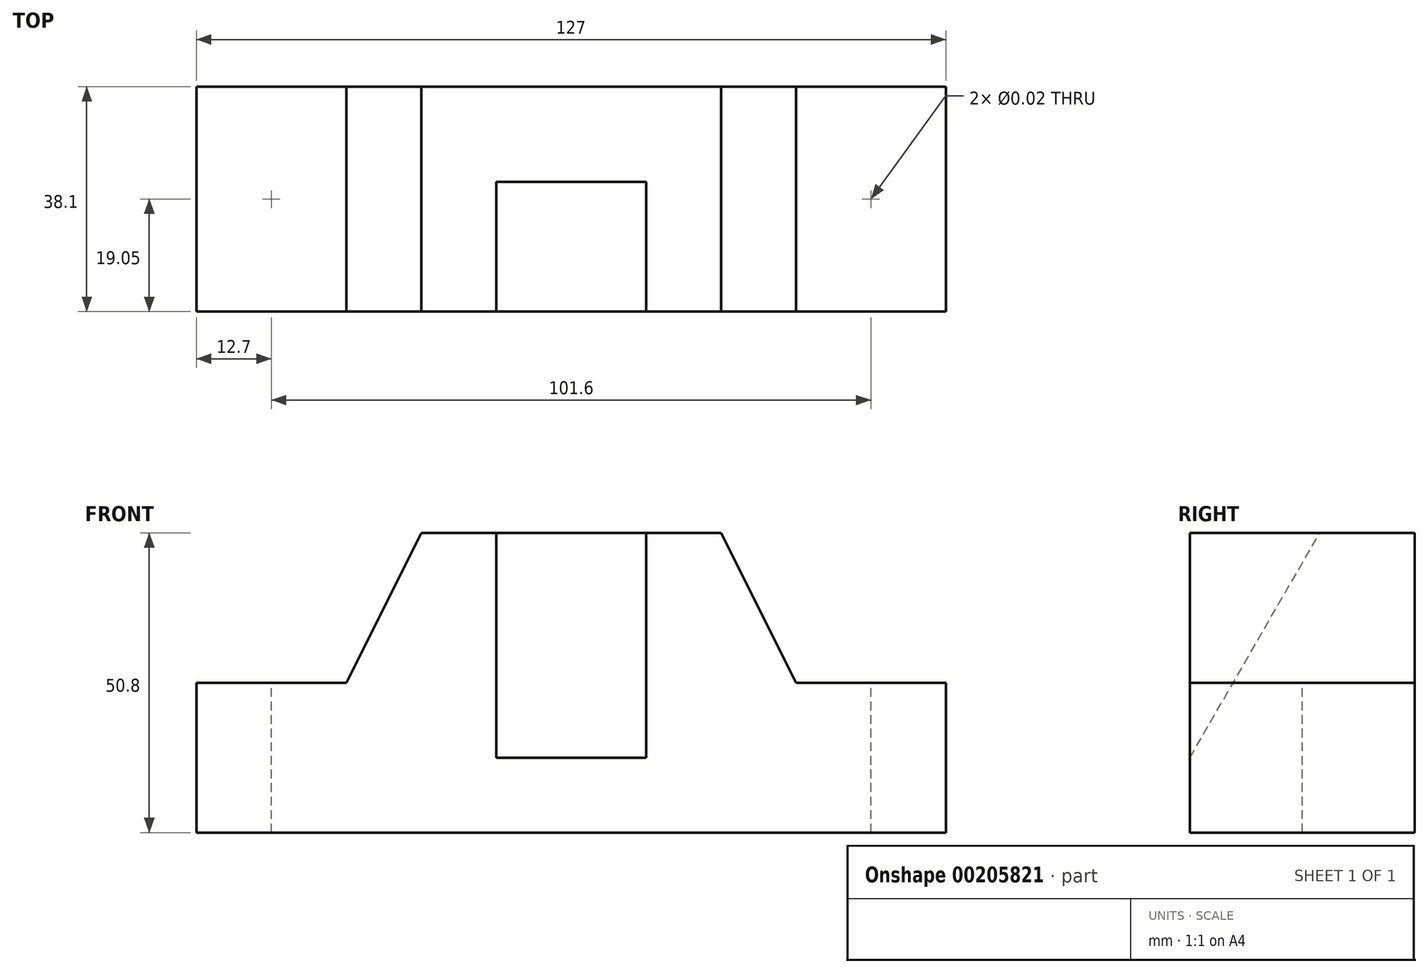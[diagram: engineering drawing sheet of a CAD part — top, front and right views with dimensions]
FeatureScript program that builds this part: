
annotation { "Feature Type Name" : "Feature", "Feature Type Description" : "" }
export const myFeature = defineFeature(function(context is Context, id is Id, definition is map)
    precondition{}
    {
        {
            var Q0;
            Q0=qCreatedBy(makeId("Front.planeOp"),FACE);
            var sketch = newSketch(context, id + "F0", { "sketchPlane" : qUnion([Q0])});
            skLineSegment(sketch, "E0", {"start": v(63.5, 0) * mm, "end": v(-63.5, 0) * mm});
            skLineSegment(sketch, "E1", {"start": v(-63.5, 0) * mm, "end": v(-63.5, 25.4) * mm});
            skLineSegment(sketch, "E2", {"start": v(-63.5, 25.4) * mm, "end": v(-38.1, 25.4) * mm});
            skLineSegment(sketch, "E3", {"start": v(-38.1, 25.4) * mm, "end": v(-25.4, 50.8) * mm});
            skLineSegment(sketch, "E4", {"start": v(-25.4, 50.8) * mm, "end": v(25.4, 50.8) * mm});
            skLineSegment(sketch, "E5", {"start": v(25.4, 50.8) * mm, "end": v(38.1, 25.4) * mm});
            skLineSegment(sketch, "E6", {"start": v(38.1, 25.4) * mm, "end": v(63.5, 25.4) * mm});
            skLineSegment(sketch, "E7", {"start": v(63.5, 25.4) * mm, "end": v(63.5, 0) * mm});
            skLineSegment(sketch, "E8", {"start": v(0, 50.8) * mm, "end": v(0, -51.26) * mm, "construction": true});
            skSolve(sketch);
        }
        {
            var Q0;
            Q0=makeQuery(id+"F0.imprint","IMPRINT",FACE,{"disambiguationData":[TD([[makeQuery(id+"F0.imprint","IMPRINT",EDGE,{"derivedFrom":sQuery(id+"F0.wireOp",EDGE,"E0")}),-1.0]])]});
            extrude(context, id + "F1", {"entities" : qUnion([Q0]), "oppositeDirection" : true, "depth" : 38.1 * mm, "offsetDistance" : 25.4 * mm});
        }
        {
            var Q0;
            Q0=makeQuery(id+"F1.opExtrude","SWEPT_FACE",FACE,{"disambiguationData":[OSD([sQuery(id+"F0.wireOp",EDGE,"E2")])]});
            var sketch = newSketch(context, id + "F2", { "sketchPlane" : qUnion([Q0])});
            skPoint(sketch, "E9", {"position": v(-50.8, 19.05) * mm});
            skPoint(sketch, "E10", {"position": v(50.8, 19.05) * mm});
            skSolve(sketch);
        }
        {
            var Q0;
            Q0=sQuery(id+"F2.wireOp",VERTEX,"E9");
            var Q1;
            Q1=sQuery(id+"F2.wireOp",VERTEX,"E10");
            var Q2;
            Q2=makeQuery(id+"F1.opExtrude","SWEPT_BODY",BODY,{"disambiguationData":[OSD([sQuery(id+"F0.wireOp",EDGE,"E0"),sQuery(id+"F0.wireOp",EDGE,"E1"),sQuery(id+"F0.wireOp",EDGE,"E2"),sQuery(id+"F0.wireOp",EDGE,"E3"),sQuery(id+"F0.wireOp",EDGE,"E4"),sQuery(id+"F0.wireOp",EDGE,"E5"),sQuery(id+"F0.wireOp",EDGE,"E6"),sQuery(id+"F0.wireOp",EDGE,"E7")])]});
            hole(context, id + "F3", {"style" : HoleStyle.SIMPLE, "endStyle" : HoleEndStyle.THROUGH, "standardTappedOrClearance" : lookupTablePath({ "standard" : "ANSI", "size" : "1/2 (0.5)", "type" : "Drilled" }), "standardBlindInLast" : lookupTablePath({ "standard" : "ANSI", "size" : "1/2 (0.5)", "type" : "Drilled" }), "holeDiameter" : 1 / 50.8 * mm, "majorDiameter" : 6.35 * mm, "isTappedThrough" : true, "tappedDepth" : 8.9 * mm, "tapClearance" : 3, "locations" : qUnion([Q0, Q1]), "scope" : qUnion([Q2])});
        }
        {
            var Q0;
            Q0=makeQuery(id+"F1.opExtrude","SWEPT_FACE",FACE,{"disambiguationData":[OSD([sQuery(id+"F0.wireOp",EDGE,"E7")])]});
            var sketch = newSketch(context, id + "F4", { "sketchPlane" : qUnion([Q0])});
            skLineSegment(sketch, "E11", {"start": v(0, 12.7) * mm, "end": v(22, 50.8) * mm});
            skLineSegment(sketch, "E12", {"start": v(22, 50.8) * mm, "end": v(0, 50.8) * mm});
            skLineSegment(sketch, "E13", {"start": v(0, 50.8) * mm, "end": v(0, 12.7) * mm});
            skSolve(sketch);
        }
        {
            var Q0;
            {var subQ0=sQuery(id+"F4.wireOp",EDGE,"E12");Q0=makeQuery(id+"F4.imprint","IMPRINT",FACE,{"disambiguationData":[TD([[makeQuery(id+"F4.imprint","IMPRINT",EDGE,{"derivedFrom":subQ0}),1.0]])]});}
            var Q1;
            {var subQ0=sQuery(id+"F4.wireOp",EDGE,"E13");var subQ1=sQuery(id+"F4.wireOp",EDGE,"E11");var subQ2=sQuery(id+"F0.wireOp",EDGE,"E7");var subQ3=makeQuery(id+"F4.imprint","INTERSECT",VERTEX,{"derivedFrom":[makeQuery(id+"F1.opExtrude","CAP_EDGE",EDGE,{"disambiguationData":[OSD([subQ2])],"isStart":true}),subQ1,subQ0]});Q1=makeQuery(id+"F4.imprint","IMPRINT",FACE,{"disambiguationData":[TD([[makeQuery(id+"F4.imprint","IMPRINT",EDGE,{"disambiguationData":[TD([[subQ3,-1.0]])],"derivedFrom":subQ1}),1.0]])]});}
            extrude(context, id + "F5", {"entities" : qUnion([Q0, Q1]), "operationType" : NewBodyOperationType.REMOVE, "oppositeDirection" : true, "depth" : 76.2 * mm, "offsetDistance" : 25.4 * mm, "hasSecondDirection" : true, "secondDirectionOppositeDirection" : true, "secondDirectionDepth" : 50.8 * mm});
        }
    });
